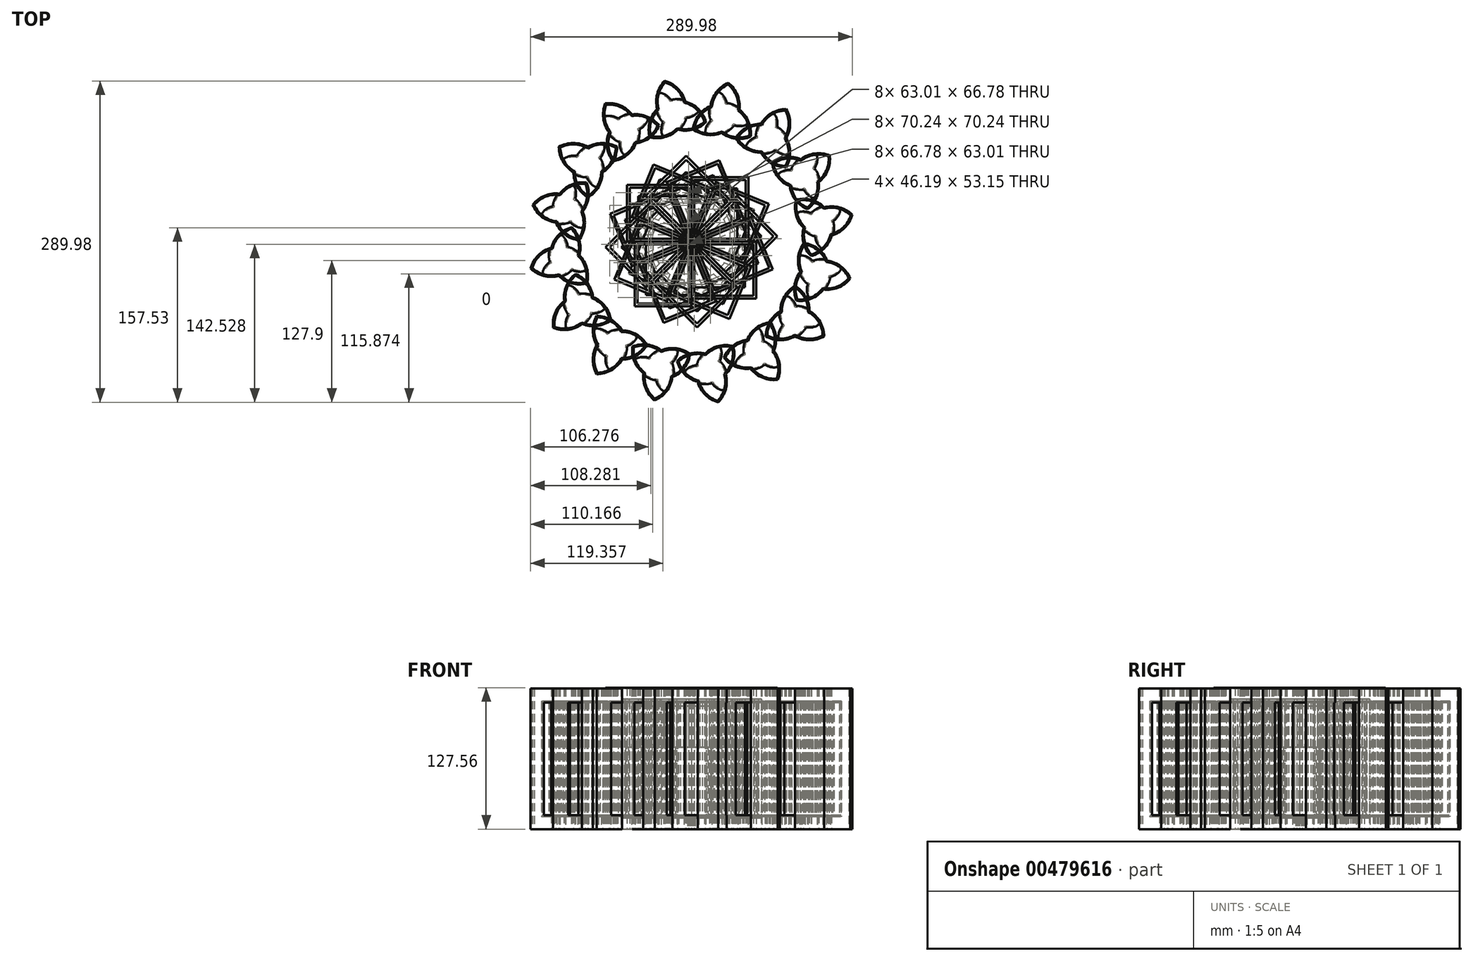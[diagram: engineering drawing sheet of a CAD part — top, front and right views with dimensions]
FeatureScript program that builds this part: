
annotation { "Feature Type Name" : "Feature", "Feature Type Description" : "" }
export const myFeature = defineFeature(function(context is Context, id is Id, definition is map)
    precondition{}
    {
        {
            var Q0;
            Q0=qCreatedBy(makeId("Top.planeOp"),FACE);
            var sketch = newSketch(context, id + "F0", { "sketchPlane" : qUnion([Q0])});
            skCircle(sketch, "E0", {"center": v(0, 0) * mm, "radius": 26.29 * mm});
            skCircle(sketch, "E1", {"center": v(26.29, 0) * mm, "radius": 26.29 * mm});
            skCircle(sketch, "E2", {"center": v(13.14, -22.77) * mm, "radius": 26.29 * mm});
            skSolve(sketch);
        }
        {
            var Q0;
            {var subQ0=sQuery(id+"F0.wireOp",EDGE,"E1");var subQ1=sQuery(id+"F0.wireOp",EDGE,"E0");var subQ2=makeQuery(id+"F0.imprint","INTERSECT",VERTEX,{"disambiguationData":[OD(0.0)],"derivedFrom":[subQ1,subQ0]});Q0=makeQuery(id+"F0.imprint","IMPRINT",FACE,{"disambiguationData":[TD([[makeQuery(id+"F0.imprint","IMPRINT",EDGE,{"disambiguationData":[TD([[subQ2,1.0]])],"derivedFrom":subQ1}),1.0]])]});}
            var Q1;
            {var subQ0=sQuery(id+"F0.wireOp",EDGE,"E2");var subQ1=sQuery(id+"F0.wireOp",EDGE,"E0");var subQ2=makeQuery(id+"F0.imprint","INTERSECT",VERTEX,{"disambiguationData":[OD(1.0)],"derivedFrom":[subQ1,subQ0]});Q1=makeQuery(id+"F0.imprint","IMPRINT",FACE,{"disambiguationData":[TD([[makeQuery(id+"F0.imprint","IMPRINT",EDGE,{"disambiguationData":[TD([[subQ2,1.0]])],"derivedFrom":subQ1}),-1.0]])]});}
            var Q2;
            {var subQ0=sQuery(id+"F0.wireOp",EDGE,"E2");var subQ1=sQuery(id+"F0.wireOp",EDGE,"E0");var subQ2=makeQuery(id+"F0.imprint","INTERSECT",VERTEX,{"disambiguationData":[OD(0.0)],"derivedFrom":[subQ1,subQ0]});Q2=makeQuery(id+"F0.imprint","IMPRINT",FACE,{"disambiguationData":[TD([[makeQuery(id+"F0.imprint","IMPRINT",EDGE,{"disambiguationData":[TD([[subQ2,-1.0]])],"derivedFrom":subQ1}),1.0]])]});}
            var Q3;
            {var subQ0=sQuery(id+"F0.wireOp",EDGE,"E2");var subQ1=sQuery(id+"F0.wireOp",EDGE,"E0");var subQ2=makeQuery(id+"F0.imprint","INTERSECT",VERTEX,{"disambiguationData":[OD(1.0)],"derivedFrom":[subQ1,subQ0]});Q3=makeQuery(id+"F0.imprint","IMPRINT",FACE,{"disambiguationData":[TD([[makeQuery(id+"F0.imprint","IMPRINT",EDGE,{"disambiguationData":[TD([[subQ2,1.0]])],"derivedFrom":subQ1}),1.0]])]});}
            extrude(context, id + "F1", {"entities" : qUnion([Q0, Q1, Q2, Q3]), "depth" : 127 * mm});
        }
        {
            var Q0;
            Q0=qCreatedBy(makeId("Top.planeOp"),FACE);
            var sketch = newSketch(context, id + "F2", { "sketchPlane" : qUnion([Q0])});
            skLineSegment(sketch, "E3.bottom", {"start": v(-21.93, 62.7) * mm, "end": v(-80.16, 62.7) * mm});
            skLineSegment(sketch, "E3.top", {"start": v(-21.93, 11.42) * mm, "end": v(-80.16, 11.42) * mm});
            skLineSegment(sketch, "E3.left", {"start": v(-21.93, 62.7) * mm, "end": v(-21.93, 11.42) * mm});
            skLineSegment(sketch, "E3.right", {"start": v(-80.16, 62.7) * mm, "end": v(-80.16, 11.42) * mm});
            skPoint(sketch, "E3.middle", {"position": v(-51.04, 37.06) * mm});
            skSolve(sketch);
        }
        {
            var Q0;
            Q0 = qSketchRegion(id + "F2", true);
            extrude(context, id + "F3", {"entities" : qUnion([Q0]), "depth" : 86.62 * mm});
        }
        {
            var Q0;
            Q0=makeQuery(id+"F3.opExtrude","SWEPT_FACE",FACE,{"disambiguationData":[OSD([sQuery(id+"F2.wireOp",EDGE,"E3.bottom")])]});
            var Q1;
            Q1=makeQuery(id+"F3.opExtrude","SWEPT_FACE",FACE,{"disambiguationData":[OSD([sQuery(id+"F2.wireOp",EDGE,"E3.right")])]});
            shell(context, id + "F4", {"entities" : qUnion([Q0, Q1]), "thickness" : 12.7 * mm});
        }
        {
            var Q0;
            {var subQ0=sQuery(id+"F0.wireOp",EDGE,"E1");Q0=makeQuery(id+"F1.opExtrude","SWEPT_FACE",FACE,{"disambiguationData":[OSD([subQ0]),TDD([makeQuery(id+"F0.imprint","IMPRINT",EDGE,{"disambiguationData":[TD([[makeQuery(id+"F0.imprint","INTERSECT",VERTEX,{"disambiguationData":[OD(0.0)],"derivedFrom":[sQuery(id+"F0.wireOp",EDGE,"E0"),subQ0]}),-1.0]])],"derivedFrom":subQ0})])]});}
            var Q1;
            {var subQ0=sQuery(id+"F0.wireOp",EDGE,"E0");Q1=makeQuery(id+"F1.opExtrude","SWEPT_FACE",FACE,{"disambiguationData":[OSD([subQ0]),TDD([makeQuery(id+"F0.imprint","IMPRINT",EDGE,{"disambiguationData":[TD([[makeQuery(id+"F0.imprint","INTERSECT",VERTEX,{"disambiguationData":[OD(0.0)],"derivedFrom":[subQ0,sQuery(id+"F0.wireOp",EDGE,"E2")]}),-1.0]])],"derivedFrom":subQ0})])]});}
            var Q2;
            {var subQ0=sQuery(id+"F0.wireOp",EDGE,"E2");Q2=makeQuery(id+"F1.opExtrude","SWEPT_FACE",FACE,{"disambiguationData":[OSD([subQ0]),TDD([makeQuery(id+"F0.imprint","IMPRINT",EDGE,{"disambiguationData":[TD([[makeQuery(id+"F0.imprint","INTERSECT",VERTEX,{"disambiguationData":[OD(0.0)],"derivedFrom":[sQuery(id+"F0.wireOp",EDGE,"E1"),subQ0]}),-1.0]])],"derivedFrom":subQ0})])]});}
            shell(context, id + "F5", {"entities" : qUnion([Q0, Q1, Q2]), "thickness" : 12.7 * mm});
        }
        {
            var Q0;
            Q0=makeQuery(id+"F1.opExtrude","CAP_FACE",FACE,{"disambiguationData":[OSD([sQuery(id+"F0.wireOp",EDGE,"E0"),sQuery(id+"F0.wireOp",EDGE,"E1"),sQuery(id+"F0.wireOp",EDGE,"E2")])],"isStart":false});
            var Q1;
            Q1=makeQuery(id+"F1.opExtrude","CAP_FACE",FACE,{"disambiguationData":[OSD([sQuery(id+"F0.wireOp",EDGE,"E0"),sQuery(id+"F0.wireOp",EDGE,"E1"),sQuery(id+"F0.wireOp",EDGE,"E2")])],"isStart":true});
            shell(context, id + "F6", {"entities" : qUnion([Q0, Q1]), "thickness" : 1.27 * mm});
        }
        {
            var Q0;
            Q0=makeQuery(id+"F3.opExtrude","CAP_FACE",FACE,{"disambiguationData":[OSD([sQuery(id+"F2.wireOp",EDGE,"E3.bottom"),sQuery(id+"F2.wireOp",EDGE,"E3.top"),sQuery(id+"F2.wireOp",EDGE,"E3.left"),sQuery(id+"F2.wireOp",EDGE,"E3.right")])],"isStart":true});
            var Q1;
            Q1=makeQuery(id+"F3.opExtrude","CAP_FACE",FACE,{"disambiguationData":[OSD([sQuery(id+"F2.wireOp",EDGE,"E3.bottom"),sQuery(id+"F2.wireOp",EDGE,"E3.top"),sQuery(id+"F2.wireOp",EDGE,"E3.left"),sQuery(id+"F2.wireOp",EDGE,"E3.right")])],"isStart":false});
            shell(context, id + "F7", {"entities" : qUnion([Q0, Q1]), "thickness" : 2.54 * mm});
        }
        {
            var Q0;
            Q0=makeQuery(id+"F1.opExtrude","SWEPT_BODY",BODY,{"disambiguationData":[OSD([sQuery(id+"F0.wireOp",EDGE,"E0"),sQuery(id+"F0.wireOp",EDGE,"E1"),sQuery(id+"F0.wireOp",EDGE,"E2")])]});
            var Q1;
            Q1=makeQuery(id+"F3.opExtrude","SWEPT_EDGE",EDGE,{"disambiguationData":[OSD([sQuery(id+"F2.wireOp",EDGE,"E3.bottom"),sQuery(id+"F2.wireOp",EDGE,"E3.right")])]});
            circularPattern(context, id + "F8", {"entities" : qUnion([Q0]), "axis" : qUnion([Q1]), "angle" : 360 * degree, "instanceCount" : 16, "equalSpace" : true});
        }
        {
            var Q0;
            {var subQ0=sQuery(id+"F2.wireOp",EDGE,"E3.right");var subQ1=sQuery(id+"F2.wireOp",EDGE,"E3.left");var subQ2=sQuery(id+"F2.wireOp",EDGE,"E3.top");var subQ3=sQuery(id+"F2.wireOp",EDGE,"E3.bottom");Q0=makeQuery(id+"F7.opShell","OFFSET_FACE",FACE,{"disambiguationData":[OSD([subQ3,subQ2,subQ1,subQ0]),TDD([makeQuery(id+"F4.opShell","OFFSET_FACE",FACE,{"disambiguationData":[OSD([subQ3,subQ2,subQ1,subQ0]),TDD([makeQuery(id+"F3.opExtrude","CAP_FACE",FACE,{"disambiguationData":[OSD([subQ3,subQ2,subQ1,subQ0])],"isStart":false})])]})])]});}
            var Q1;
            Q1=makeQuery(id+"F3.opExtrude","CAP_FACE",FACE,{"disambiguationData":[OSD([sQuery(id+"F2.wireOp",EDGE,"E3.bottom"),sQuery(id+"F2.wireOp",EDGE,"E3.top"),sQuery(id+"F2.wireOp",EDGE,"E3.left"),sQuery(id+"F2.wireOp",EDGE,"E3.right")])],"isStart":false});
            extrude(context, id + "F9", {"entities" : qUnion([Q0, Q1]), "operationType" : NewBodyOperationType.ADD, "depth" : 40.94 * mm});
        }
        {
            var Q0;
            {var subQ0=sQuery(id+"F2.wireOp",EDGE,"E3.right");var subQ1=sQuery(id+"F2.wireOp",EDGE,"E3.left");var subQ2=sQuery(id+"F2.wireOp",EDGE,"E3.top");var subQ3=sQuery(id+"F2.wireOp",EDGE,"E3.bottom");Q0=makeQuery(id+"F4.opShell","OFFSET_FACE",FACE,{"disambiguationData":[OSD([subQ3,subQ2,subQ1,subQ0]),TDD([makeQuery(id+"F3.opExtrude","CAP_FACE",FACE,{"disambiguationData":[OSD([subQ3,subQ2,subQ1,subQ0])],"isStart":false})])]});}
            var Q1;
            {var subQ0=sQuery(id+"F2.wireOp",EDGE,"E3.right");Q1=makeQuery(id+"F9.boolean.opBoolean","MERGE",FACE,{"derivedFrom":[makeQuery(id+"F3.opExtrude","SWEPT_FACE",FACE,{"disambiguationData":[OSD([subQ0])]}),makeQuery(id+"F9.opExtrude","SWEPT_FACE",FACE,{"disambiguationData":[OSD([subQ0]),TDD([makeQuery(id+"F3.opExtrude","CAP_EDGE",EDGE,{"disambiguationData":[OSD([subQ0])],"isStart":false})])]})]});}
            shell(context, id + "F10", {"entities" : qUnion([Q0, Q1]), "thickness" : 6.35 * mm});
        }
        {
            var Q0;
            Q0=makeQuery(id+"F3.opExtrude","SWEPT_BODY",BODY,{"disambiguationData":[OSD([sQuery(id+"F2.wireOp",EDGE,"E3.bottom"),sQuery(id+"F2.wireOp",EDGE,"E3.top"),sQuery(id+"F2.wireOp",EDGE,"E3.left"),sQuery(id+"F2.wireOp",EDGE,"E3.right")])]});
            var Q1;
            Q1=makeQuery(id+"F4.opShell","OFFSET_EDGE",EDGE,{"disambiguationData":[OSD([sQuery(id+"F2.wireOp",EDGE,"E3.bottom"),sQuery(id+"F2.wireOp",EDGE,"E3.right")])]});
            circularPattern(context, id + "F11", {"entities" : qUnion([Q0]), "axis" : qUnion([Q1]), "angle" : 360 * degree, "instanceCount" : 16, "oppositeDirection" : true, "equalSpace" : true, "isCentered" : true});
        }
    });
